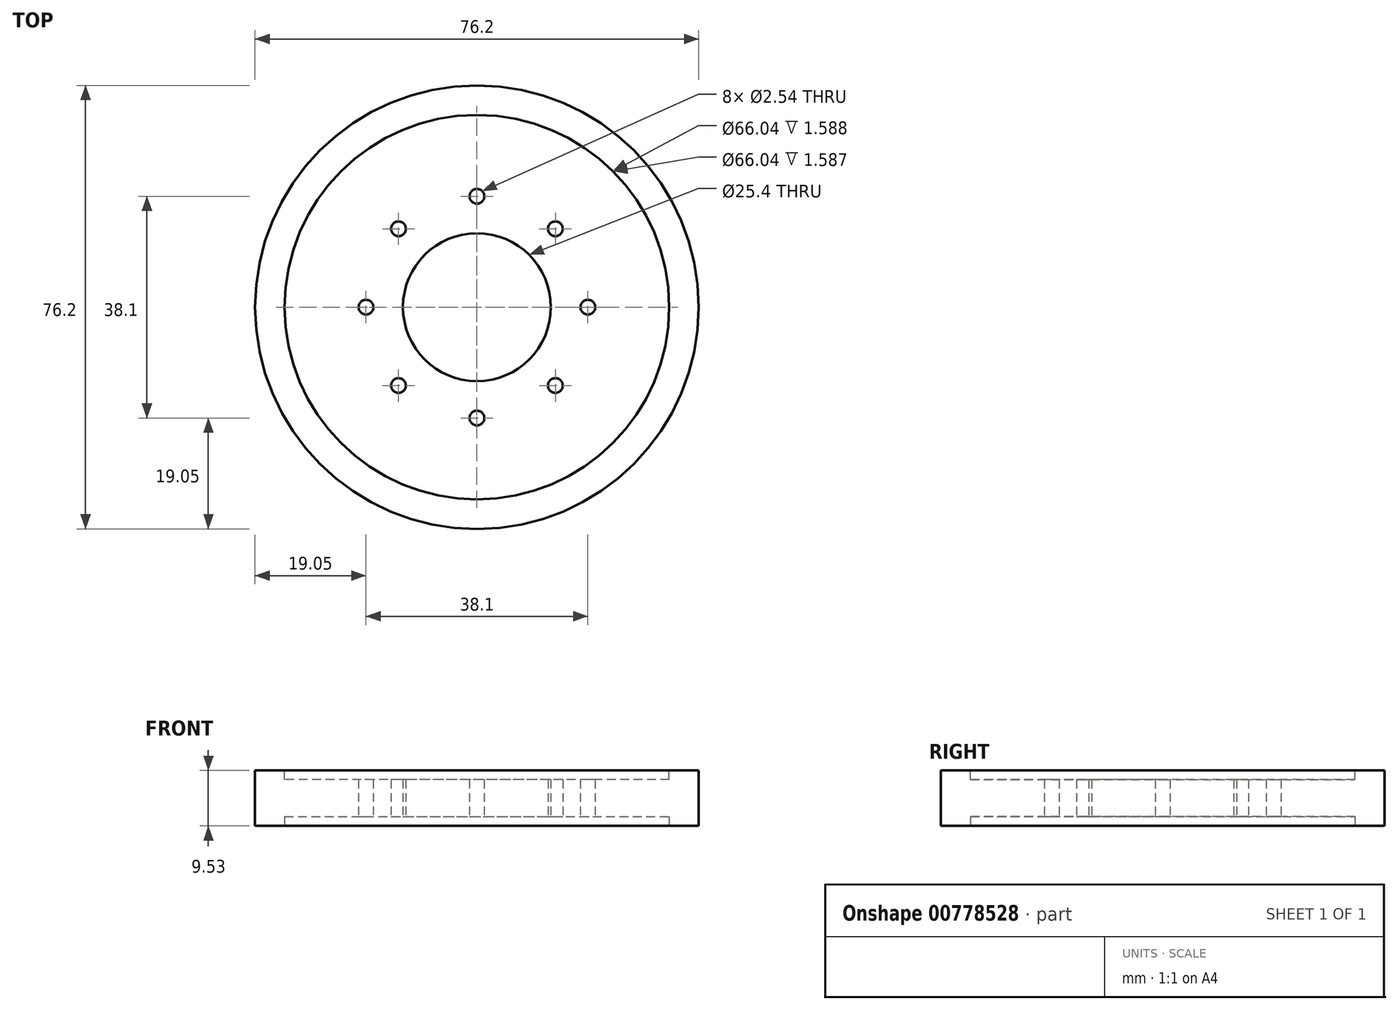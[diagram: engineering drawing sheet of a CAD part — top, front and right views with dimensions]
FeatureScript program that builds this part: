
annotation { "Feature Type Name" : "Feature", "Feature Type Description" : "" }
export const myFeature = defineFeature(function(context is Context, id is Id, definition is map)
    precondition{}
    {
        {
            var Q0;
            Q0=qCreatedBy(makeId("Top.planeOp"),FACE);
            var sketch = newSketch(context, id + "F0", { "sketchPlane" : qUnion([Q0])});
            skCircle(sketch, "E0", {"center": v(0, 0) * mm, "radius": 38.1 * mm});
            skSolve(sketch);
        }
        {
            var Q0;
            Q0 = qSketchRegion(id + "F0", true);
            extrude(context, id + "F1", {"entities" : qUnion([Q0]), "depth" : 9.52 * mm, "offsetDistance" : 25.4 * mm});
        }
        {
            var Q0;
            Q0=makeQuery(id+"F1.opExtrude","CAP_FACE",FACE,{"disambiguationData":[OSD([sQuery(id+"F0.wireOp",EDGE,"E0")])],"isStart":false});
            var sketch = newSketch(context, id + "F2", { "sketchPlane" : qUnion([Q0])});
            skCircle(sketch, "E1", {"center": v(0, 0) * mm, "radius": 33.02 * mm});
            skSolve(sketch);
        }
        {
            var Q0;
            Q0 = qSketchRegion(id + "F2", true);
            extrude(context, id + "F3", {"entities" : qUnion([Q0]), "operationType" : NewBodyOperationType.REMOVE, "oppositeDirection" : true, "depth" : 1.59 * mm, "offsetDistance" : 25.4 * mm});
        }
        {
            var Q0;
            Q0=makeQuery(id+"F1.opExtrude","CAP_FACE",FACE,{"disambiguationData":[OSD([sQuery(id+"F0.wireOp",EDGE,"E0")])],"isStart":true});
            var sketch = newSketch(context, id + "F4", { "sketchPlane" : qUnion([Q0])});
            skCircle(sketch, "E2", {"center": v(0, 0) * mm, "radius": 33.02 * mm});
            skSolve(sketch);
        }
        {
            var Q0;
            Q0 = qSketchRegion(id + "F4", true);
            extrude(context, id + "F5", {"entities" : qUnion([Q0]), "operationType" : NewBodyOperationType.REMOVE, "oppositeDirection" : true, "depth" : 1.59 * mm, "offsetDistance" : 25.4 * mm});
        }
        {
            var Q0;
            Q0=makeQuery(id+"F5.boolean.opBoolean","COPY",FACE,{"derivedFrom":makeQuery(id+"F5.opExtrude","CAP_FACE",FACE,{"disambiguationData":[OSD([sQuery(id+"F4.wireOp",EDGE,"E2")])],"isStart":false})});
            var sketch = newSketch(context, id + "F6", { "sketchPlane" : qUnion([Q0])});
            skCircle(sketch, "E3", {"center": v(0, 0) * mm, "radius": 12.7 * mm});
            skLineSegment(sketch, "E4", {"start": v(0, 0) * mm, "end": v(-19.05, 0) * mm, "construction": true});
            skCircle(sketch, "E5", {"center": v(-19.05, 0) * mm, "radius": 1.27 * mm});
            skCircle(sketch, "E6.1.0", {"center": v(-13.47, -13.47) * mm, "radius": 1.27 * mm});
            skCircle(sketch, "E6.2.0", {"center": v(0, -19.05) * mm, "radius": 1.27 * mm});
            skCircle(sketch, "E6.3.0", {"center": v(13.47, -13.47) * mm, "radius": 1.27 * mm});
            skCircle(sketch, "E6.4.0", {"center": v(19.05, 0) * mm, "radius": 1.27 * mm});
            skCircle(sketch, "E6.5.0", {"center": v(13.47, 13.47) * mm, "radius": 1.27 * mm});
            skCircle(sketch, "E6.6.0", {"center": v(0, 19.05) * mm, "radius": 1.27 * mm});
            skCircle(sketch, "E6.7.0", {"center": v(-13.47, 13.47) * mm, "radius": 1.27 * mm});
            skSolve(sketch);
        }
        {
            var Q0;
            Q0 = qSketchRegion(id + "F6", true);
            extrude(context, id + "F7", {"entities" : qUnion([Q0]), "operationType" : NewBodyOperationType.REMOVE, "oppositeDirection" : true, "depth" : 25.4 * mm, "offsetDistance" : 25.4 * mm});
        }
    });
